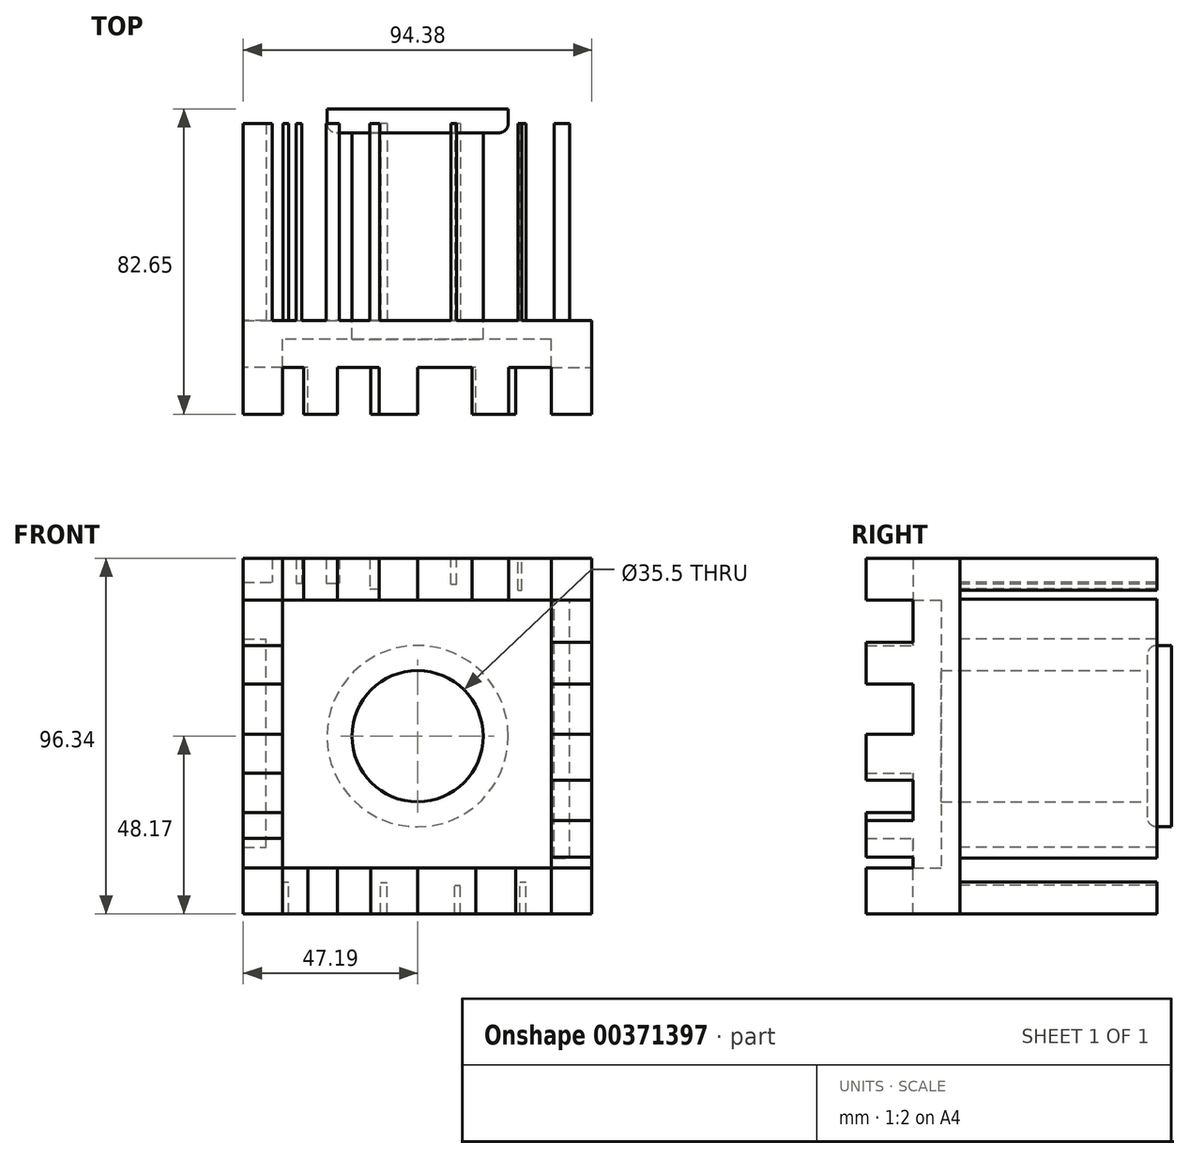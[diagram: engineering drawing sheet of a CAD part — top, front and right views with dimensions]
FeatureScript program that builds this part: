
annotation { "Feature Type Name" : "Feature", "Feature Type Description" : "" }
export const myFeature = defineFeature(function(context is Context, id is Id, definition is map)
    precondition{}
    {
        {
            var Q0;
            Q0=qCreatedBy(makeId("Front.planeOp"),FACE);
            var sketch = newSketch(context, id + "F0", { "sketchPlane" : qUnion([Q0])});
            skCircle(sketch, "E0", {"center": v(0, 0) * mm, "radius": 24.55 * mm});
            skSolve(sketch);
        }
        {
            var Q0;
            Q0 = qSketchRegion(id + "F0", true);
            extrude(context, id + "F1", {"entities" : qUnion([Q0]), "depth" : 6.45 * mm});
        }
        {
            var Q0;
            Q0=makeQuery(id+"F1.opExtrude","CAP_FACE",FACE,{"disambiguationData":[OSD([sQuery(id+"F0.wireOp",EDGE,"E0")])],"isStart":false});
            var sketch = newSketch(context, id + "F2", { "sketchPlane" : qUnion([Q0])});
            skCircle(sketch, "E1", {"center": v(0, 0) * mm, "radius": 17.75 * mm});
            skSolve(sketch);
        }
        {
            var Q0;
            Q0 = qSketchRegion(id + "F2", true);
            extrude(context, id + "F3", {"entities" : qUnion([Q0]), "operationType" : NewBodyOperationType.ADD, "depth" : 50.8 * mm});
        }
        {
            var Q0;
            Q0=makeQuery(id+"F3.opExtrude","CAP_FACE",FACE,{"disambiguationData":[OSD([sQuery(id+"F2.wireOp",EDGE,"E1")])],"isStart":false});
            var sketch = newSketch(context, id + "F4", { "sketchPlane" : qUnion([Q0])});
            skLineSegment(sketch, "E2.bottom", {"start": v(47.2, -48.17) * mm, "end": v(-47.2, -48.17) * mm});
            skLineSegment(sketch, "E2.top", {"start": v(47.2, 48.17) * mm, "end": v(-47.2, 48.17) * mm});
            skLineSegment(sketch, "E2.left", {"start": v(47.2, -48.17) * mm, "end": v(47.2, 48.17) * mm});
            skLineSegment(sketch, "E2.right", {"start": v(-47.2, -48.17) * mm, "end": v(-47.2, 48.17) * mm});
            skPoint(sketch, "E2.middle", {"position": v(0, 0) * mm});
            skSolve(sketch);
        }
        {
            var Q0;
            Q0=makeQuery(id+"F4.imprint","IMPRINT",FACE,{"disambiguationData":[TD([[makeQuery(id+"F4.imprint","IMPRINT",EDGE,{"derivedFrom":sQuery(id+"F4.wireOp",EDGE,"E2.bottom")}),-1.0]])]});
            extrude(context, id + "F5", {"entities" : qUnion([Q0]), "depth" : 5.08 * mm});
        }
        {
            var Q0;
            Q0=makeQuery(id+"F5.opExtrude","CAP_FACE",FACE,{"disambiguationData":[OSD([sQuery(id+"F2.wireOp",EDGE,"E1"),sQuery(id+"F4.wireOp",EDGE,"E2.bottom"),sQuery(id+"F4.wireOp",EDGE,"E2.top"),sQuery(id+"F4.wireOp",EDGE,"E2.left"),sQuery(id+"F4.wireOp",EDGE,"E2.right")])],"isStart":false});
            var sketch = newSketch(context, id + "F6", { "sketchPlane" : qUnion([Q0])});
            skLineSegment(sketch, "E3.bottom", {"start": v(-47.2, 48.17) * mm, "end": v(-36.6, 48.17) * mm});
            skLineSegment(sketch, "E3.top", {"start": v(-47.2, -48.17) * mm, "end": v(-36.6, -48.17) * mm});
            skLineSegment(sketch, "E3.left", {"start": v(-47.2, 48.17) * mm, "end": v(-47.2, -48.17) * mm});
            skLineSegment(sketch, "E3.right", {"start": v(-36.6, 48.17) * mm, "end": v(-36.6, -48.17) * mm});
            skLineSegment(sketch, "E4.bottom", {"start": v(47.2, -48.17) * mm, "end": v(-36.6, -48.17) * mm});
            skLineSegment(sketch, "E4.top", {"start": v(47.2, -35.68) * mm, "end": v(-36.6, -35.68) * mm});
            skLineSegment(sketch, "E4.left", {"start": v(47.2, -48.17) * mm, "end": v(47.2, -35.68) * mm});
            skLineSegment(sketch, "E4.right", {"start": v(-36.6, -48.17) * mm, "end": v(-36.6, -35.68) * mm});
            skLineSegment(sketch, "E5.bottom", {"start": v(47.2, 48.17) * mm, "end": v(-36.6, 48.17) * mm});
            skLineSegment(sketch, "E5.top", {"start": v(47.2, 36.8) * mm, "end": v(-36.6, 36.8) * mm});
            skLineSegment(sketch, "E5.left", {"start": v(47.2, 48.17) * mm, "end": v(47.2, 36.8) * mm});
            skLineSegment(sketch, "E5.right", {"start": v(-36.6, 48.17) * mm, "end": v(-36.6, 36.8) * mm});
            skLineSegment(sketch, "E6.bottom", {"start": v(47.2, 36.8) * mm, "end": v(36.19, 36.8) * mm});
            skLineSegment(sketch, "E6.top", {"start": v(47.2, -35.68) * mm, "end": v(36.19, -35.68) * mm});
            skLineSegment(sketch, "E6.left", {"start": v(47.2, 36.8) * mm, "end": v(47.2, -35.68) * mm});
            skLineSegment(sketch, "E6.right", {"start": v(36.19, 36.8) * mm, "end": v(36.19, -35.68) * mm});
            skSolve(sketch);
        }
        {
            var Q0;
            Q0 = qSketchRegion(id + "F6", true);
            extrude(context, id + "F7", {"entities" : qUnion([Q0]), "operationType" : NewBodyOperationType.ADD, "depth" : 7.62 * mm});
        }
        {
            var Q0;
            Q0=makeQuery(id+"F7.opExtrude","CAP_FACE",FACE,{"disambiguationData":[OSD([sQuery(id+"F6.wireOp",EDGE,"E3.bottom"),sQuery(id+"F6.wireOp",EDGE,"E3.top"),sQuery(id+"F6.wireOp",EDGE,"E3.left"),sQuery(id+"F6.wireOp",EDGE,"E3.right"),sQuery(id+"F6.wireOp",EDGE,"E4.bottom"),sQuery(id+"F6.wireOp",EDGE,"E4.top"),sQuery(id+"F6.wireOp",EDGE,"E4.left"),sQuery(id+"F6.wireOp",EDGE,"E5.bottom"),sQuery(id+"F6.wireOp",EDGE,"E5.top"),sQuery(id+"F6.wireOp",EDGE,"E5.left"),sQuery(id+"F6.wireOp",EDGE,"E6.left"),sQuery(id+"F6.wireOp",EDGE,"E6.right")])],"isStart":false});
            var sketch = newSketch(context, id + "F8", { "sketchPlane" : qUnion([Q0])});
            skLineSegment(sketch, "E7.bottom", {"start": v(47.2, 48.17) * mm, "end": v(36.19, 48.17) * mm});
            skLineSegment(sketch, "E7.top", {"start": v(47.2, 36.8) * mm, "end": v(36.19, 36.8) * mm});
            skLineSegment(sketch, "E7.left", {"start": v(47.2, 48.17) * mm, "end": v(47.2, 36.8) * mm});
            skLineSegment(sketch, "E7.right", {"start": v(36.19, 48.17) * mm, "end": v(36.19, 36.8) * mm});
            skLineSegment(sketch, "E8.bottom", {"start": v(24.7, 48.17) * mm, "end": v(14.71, 48.17) * mm});
            skLineSegment(sketch, "E8.top", {"start": v(24.7, 36.8) * mm, "end": v(14.71, 36.8) * mm});
            skLineSegment(sketch, "E8.left", {"start": v(24.7, 48.17) * mm, "end": v(24.7, 36.8) * mm});
            skLineSegment(sketch, "E8.right", {"start": v(14.71, 48.17) * mm, "end": v(14.71, 36.8) * mm});
            skLineSegment(sketch, "E9.bottom", {"start": v(0, 48.17) * mm, "end": v(-10.43, 48.17) * mm});
            skLineSegment(sketch, "E9.top", {"start": v(0, 36.8) * mm, "end": v(-10.43, 36.8) * mm});
            skLineSegment(sketch, "E9.left", {"start": v(0, 48.17) * mm, "end": v(0, 36.8) * mm});
            skLineSegment(sketch, "E9.right", {"start": v(-10.43, 48.17) * mm, "end": v(-10.43, 36.8) * mm});
            skLineSegment(sketch, "E10.bottom", {"start": v(-21.71, 48.17) * mm, "end": v(-30.9, 48.17) * mm});
            skLineSegment(sketch, "E10.top", {"start": v(-21.71, 36.8) * mm, "end": v(-30.9, 36.8) * mm});
            skLineSegment(sketch, "E10.left", {"start": v(-21.71, 48.17) * mm, "end": v(-21.71, 36.8) * mm});
            skLineSegment(sketch, "E10.right", {"start": v(-30.9, 48.17) * mm, "end": v(-30.9, 36.8) * mm});
            skLineSegment(sketch, "E11.bottom", {"start": v(-36.6, 36.8) * mm, "end": v(-47.2, 36.8) * mm});
            skLineSegment(sketch, "E11.top", {"start": v(-36.6, 48.17) * mm, "end": v(-47.2, 48.17) * mm});
            skLineSegment(sketch, "E11.left", {"start": v(-36.6, 36.8) * mm, "end": v(-36.6, 48.17) * mm});
            skLineSegment(sketch, "E11.right", {"start": v(-47.2, 36.8) * mm, "end": v(-47.2, 48.17) * mm});
            skLineSegment(sketch, "E12.bottom", {"start": v(-36.6, 24.51) * mm, "end": v(-47.2, 24.51) * mm});
            skLineSegment(sketch, "E12.top", {"start": v(-36.6, 14.1) * mm, "end": v(-47.2, 14.1) * mm});
            skLineSegment(sketch, "E12.left", {"start": v(-36.6, 24.51) * mm, "end": v(-36.6, 14.1) * mm});
            skLineSegment(sketch, "E12.right", {"start": v(-47.2, 24.51) * mm, "end": v(-47.2, 14.1) * mm});
            skLineSegment(sketch, "E13.bottom", {"start": v(-36.6, 0.56) * mm, "end": v(-47.2, 0.56) * mm});
            skLineSegment(sketch, "E13.top", {"start": v(-36.6, -10.02) * mm, "end": v(-47.2, -10.02) * mm});
            skLineSegment(sketch, "E13.left", {"start": v(-36.6, 0.56) * mm, "end": v(-36.6, -10.02) * mm});
            skLineSegment(sketch, "E13.right", {"start": v(-47.2, 0.56) * mm, "end": v(-47.2, -10.02) * mm});
            skLineSegment(sketch, "E14.bottom", {"start": v(-36.6, -20.68) * mm, "end": v(-47.2, -20.68) * mm});
            skLineSegment(sketch, "E14.top", {"start": v(-36.6, -27.62) * mm, "end": v(-47.2, -27.62) * mm});
            skLineSegment(sketch, "E14.left", {"start": v(-36.6, -20.68) * mm, "end": v(-36.6, -27.62) * mm});
            skLineSegment(sketch, "E14.right", {"start": v(-47.2, -20.68) * mm, "end": v(-47.2, -27.62) * mm});
            skLineSegment(sketch, "E15.bottom", {"start": v(-36.6, -35.68) * mm, "end": v(-47.2, -35.68) * mm});
            skLineSegment(sketch, "E15.top", {"start": v(-36.6, -48.17) * mm, "end": v(-47.2, -48.17) * mm});
            skLineSegment(sketch, "E15.left", {"start": v(-36.6, -35.68) * mm, "end": v(-36.6, -48.17) * mm});
            skLineSegment(sketch, "E15.right", {"start": v(-47.2, -35.68) * mm, "end": v(-47.2, -48.17) * mm});
            skLineSegment(sketch, "E16.bottom", {"start": v(36.19, 25.4) * mm, "end": v(47.2, 25.4) * mm});
            skLineSegment(sketch, "E16.top", {"start": v(36.19, 14.16) * mm, "end": v(47.2, 14.16) * mm});
            skLineSegment(sketch, "E16.left", {"start": v(36.19, 25.4) * mm, "end": v(36.19, 14.16) * mm});
            skLineSegment(sketch, "E16.right", {"start": v(47.2, 25.4) * mm, "end": v(47.2, 14.16) * mm});
            skLineSegment(sketch, "E17.bottom", {"start": v(36.19, 0.56) * mm, "end": v(47.2, 0.56) * mm});
            skLineSegment(sketch, "E17.top", {"start": v(36.19, -11.97) * mm, "end": v(47.2, -11.97) * mm});
            skLineSegment(sketch, "E17.left", {"start": v(36.19, 0.56) * mm, "end": v(36.19, -11.97) * mm});
            skLineSegment(sketch, "E17.right", {"start": v(47.2, 0.56) * mm, "end": v(47.2, -11.97) * mm});
            skLineSegment(sketch, "E18.bottom", {"start": v(36.19, -22.9) * mm, "end": v(47.2, -22.9) * mm});
            skLineSegment(sketch, "E18.top", {"start": v(36.19, -32.7) * mm, "end": v(47.2, -32.7) * mm});
            skLineSegment(sketch, "E18.left", {"start": v(36.19, -22.9) * mm, "end": v(36.19, -32.7) * mm});
            skLineSegment(sketch, "E18.right", {"start": v(47.2, -22.9) * mm, "end": v(47.2, -32.7) * mm});
            skLineSegment(sketch, "E19.bottom", {"start": v(47.2, -48.17) * mm, "end": v(36.19, -48.17) * mm});
            skLineSegment(sketch, "E19.top", {"start": v(47.2, -35.68) * mm, "end": v(36.19, -35.68) * mm});
            skLineSegment(sketch, "E19.left", {"start": v(47.2, -48.17) * mm, "end": v(47.2, -35.68) * mm});
            skLineSegment(sketch, "E19.right", {"start": v(36.19, -48.17) * mm, "end": v(36.19, -35.68) * mm});
            skLineSegment(sketch, "E20.bottom", {"start": v(26.62, -48.17) * mm, "end": v(15.76, -48.17) * mm});
            skLineSegment(sketch, "E20.top", {"start": v(26.62, -35.68) * mm, "end": v(15.76, -35.68) * mm});
            skLineSegment(sketch, "E20.left", {"start": v(26.62, -48.17) * mm, "end": v(26.62, -35.68) * mm});
            skLineSegment(sketch, "E20.right", {"start": v(15.76, -48.17) * mm, "end": v(15.76, -35.68) * mm});
            skLineSegment(sketch, "E21.bottom", {"start": v(0, -48.17) * mm, "end": v(-12.67, -48.17) * mm});
            skLineSegment(sketch, "E21.top", {"start": v(0, -35.68) * mm, "end": v(-12.67, -35.68) * mm});
            skLineSegment(sketch, "E21.left", {"start": v(0, -48.17) * mm, "end": v(0, -35.68) * mm});
            skLineSegment(sketch, "E21.right", {"start": v(-12.67, -48.17) * mm, "end": v(-12.67, -35.68) * mm});
            skLineSegment(sketch, "E22.bottom", {"start": v(-21.71, -48.17) * mm, "end": v(-29.71, -48.17) * mm});
            skLineSegment(sketch, "E22.top", {"start": v(-21.71, -35.68) * mm, "end": v(-29.71, -35.68) * mm});
            skLineSegment(sketch, "E22.left", {"start": v(-21.71, -48.17) * mm, "end": v(-21.71, -35.68) * mm});
            skLineSegment(sketch, "E22.right", {"start": v(-29.71, -48.17) * mm, "end": v(-29.71, -35.68) * mm});
            skSolve(sketch);
        }
        {
            var Q0;
            Q0 = qSketchRegion(id + "F8", true);
            extrude(context, id + "F9", {"entities" : qUnion([Q0]), "operationType" : NewBodyOperationType.ADD, "depth" : 12.7 * mm});
        }
        {
            var Q0;
            Q0=makeQuery(id+"F5.opExtrude","CAP_FACE",FACE,{"disambiguationData":[OSD([sQuery(id+"F2.wireOp",EDGE,"E1"),sQuery(id+"F4.wireOp",EDGE,"E2.bottom"),sQuery(id+"F4.wireOp",EDGE,"E2.top"),sQuery(id+"F4.wireOp",EDGE,"E2.left"),sQuery(id+"F4.wireOp",EDGE,"E2.right")])],"isStart":true});
            var sketch = newSketch(context, id + "F10", { "sketchPlane" : qUnion([Q0])});
            skLineSegment(sketch, "E23.bottom", {"start": v(9.95, -48.17) * mm, "end": v(8.18, -48.17) * mm});
            skLineSegment(sketch, "E23.top", {"start": v(9.95, -39.55) * mm, "end": v(8.18, -39.55) * mm});
            skLineSegment(sketch, "E23.left", {"start": v(9.95, -48.17) * mm, "end": v(9.95, -39.55) * mm});
            skLineSegment(sketch, "E23.right", {"start": v(8.18, -48.17) * mm, "end": v(8.18, -39.55) * mm});
            skLineSegment(sketch, "E24.bottom", {"start": v(-10.05, -48.17) * mm, "end": v(-11.57, -48.17) * mm});
            skLineSegment(sketch, "E24.top", {"start": v(-10.05, -40.4) * mm, "end": v(-11.57, -40.4) * mm});
            skLineSegment(sketch, "E24.left", {"start": v(-10.05, -48.17) * mm, "end": v(-10.05, -40.4) * mm});
            skLineSegment(sketch, "E24.right", {"start": v(-11.57, -48.17) * mm, "end": v(-11.57, -40.4) * mm});
            skLineSegment(sketch, "E25.bottom", {"start": v(-27.74, -48.17) * mm, "end": v(-29.37, -48.17) * mm});
            skLineSegment(sketch, "E25.top", {"start": v(-27.74, -39.52) * mm, "end": v(-29.37, -39.52) * mm});
            skLineSegment(sketch, "E25.left", {"start": v(-27.74, -48.17) * mm, "end": v(-27.74, -39.52) * mm});
            skLineSegment(sketch, "E25.right", {"start": v(-29.37, -48.17) * mm, "end": v(-29.37, -39.52) * mm});
            skLineSegment(sketch, "E26.bottom", {"start": v(36.38, -48.17) * mm, "end": v(34.96, -48.17) * mm});
            skLineSegment(sketch, "E26.top", {"start": v(36.38, -39.45) * mm, "end": v(34.96, -39.45) * mm});
            skLineSegment(sketch, "E26.left", {"start": v(36.38, -48.17) * mm, "end": v(36.38, -39.45) * mm});
            skLineSegment(sketch, "E26.right", {"start": v(34.96, -48.17) * mm, "end": v(34.96, -39.45) * mm});
            skLineSegment(sketch, "E27.bottom", {"start": v(-27.2, 39.51) * mm, "end": v(-28.2, 39.51) * mm});
            skLineSegment(sketch, "E27.top", {"start": v(-27.2, 48.17) * mm, "end": v(-28.2, 48.17) * mm});
            skLineSegment(sketch, "E27.left", {"start": v(-27.2, 39.51) * mm, "end": v(-27.2, 48.17) * mm});
            skLineSegment(sketch, "E27.right", {"start": v(-28.2, 39.51) * mm, "end": v(-28.2, 48.17) * mm});
            skLineSegment(sketch, "E28.bottom", {"start": v(-9.07, 41.1) * mm, "end": v(-10.58, 41.1) * mm});
            skLineSegment(sketch, "E28.top", {"start": v(-9.07, 48.17) * mm, "end": v(-10.58, 48.17) * mm});
            skLineSegment(sketch, "E28.left", {"start": v(-9.07, 41.1) * mm, "end": v(-9.07, 48.17) * mm});
            skLineSegment(sketch, "E28.right", {"start": v(-10.58, 41.1) * mm, "end": v(-10.58, 48.17) * mm});
            skLineSegment(sketch, "E29.bottom", {"start": v(47.2, 48.17) * mm, "end": v(39.32, 48.17) * mm});
            skLineSegment(sketch, "E29.top", {"start": v(47.2, 41.64) * mm, "end": v(39.32, 41.64) * mm});
            skLineSegment(sketch, "E29.left", {"start": v(47.2, 48.17) * mm, "end": v(47.2, 41.64) * mm});
            skLineSegment(sketch, "E29.right", {"start": v(39.32, 48.17) * mm, "end": v(39.32, 41.64) * mm});
            skLineSegment(sketch, "E30.bottom", {"start": v(32.94, 48.17) * mm, "end": v(31.32, 48.17) * mm});
            skLineSegment(sketch, "E30.top", {"start": v(32.94, 41.42) * mm, "end": v(31.32, 41.42) * mm});
            skLineSegment(sketch, "E30.left", {"start": v(32.94, 48.17) * mm, "end": v(32.94, 41.42) * mm});
            skLineSegment(sketch, "E30.right", {"start": v(31.32, 48.17) * mm, "end": v(31.32, 41.42) * mm});
            skLineSegment(sketch, "E31.bottom", {"start": v(24.76, 48.17) * mm, "end": v(21.16, 48.17) * mm});
            skLineSegment(sketch, "E31.top", {"start": v(24.76, 41.42) * mm, "end": v(21.16, 41.42) * mm});
            skLineSegment(sketch, "E31.left", {"start": v(24.76, 48.17) * mm, "end": v(24.76, 41.42) * mm});
            skLineSegment(sketch, "E31.right", {"start": v(21.16, 48.17) * mm, "end": v(21.16, 41.42) * mm});
            skLineSegment(sketch, "E32.bottom", {"start": v(12.96, 48.17) * mm, "end": v(10.26, 48.17) * mm});
            skLineSegment(sketch, "E32.top", {"start": v(12.96, 39.85) * mm, "end": v(10.26, 39.85) * mm});
            skLineSegment(sketch, "E32.left", {"start": v(12.96, 48.17) * mm, "end": v(12.96, 39.85) * mm});
            skLineSegment(sketch, "E32.right", {"start": v(10.26, 48.17) * mm, "end": v(10.26, 39.85) * mm});
            skLineSegment(sketch, "E33.bottom", {"start": v(-37.02, -33.02) * mm, "end": v(-41.14, -33.02) * mm});
            skLineSegment(sketch, "E33.top", {"start": v(-37.02, 37.05) * mm, "end": v(-41.14, 37.05) * mm});
            skLineSegment(sketch, "E33.left", {"start": v(-37.02, -33.02) * mm, "end": v(-37.02, 37.05) * mm});
            skLineSegment(sketch, "E33.right", {"start": v(-41.14, -33.02) * mm, "end": v(-41.14, 37.05) * mm});
            skLineSegment(sketch, "E34.bottom", {"start": v(47.2, -30.1) * mm, "end": v(41.02, -30.1) * mm});
            skLineSegment(sketch, "E34.top", {"start": v(47.2, 26.3) * mm, "end": v(41.02, 26.3) * mm});
            skLineSegment(sketch, "E34.left", {"start": v(47.2, -30.1) * mm, "end": v(47.2, 26.3) * mm});
            skLineSegment(sketch, "E34.right", {"start": v(41.02, -30.1) * mm, "end": v(41.02, 26.3) * mm});
            skSolve(sketch);
        }
        {
            var Q0;
            Q0=makeQuery(id+"F10.imprint","IMPRINT",FACE,{"disambiguationData":[TD([[makeQuery(id+"F10.imprint","IMPRINT",EDGE,{"derivedFrom":sQuery(id+"F10.wireOp",EDGE,"E34.bottom")}),-1.0]])]});
            var Q1;
            Q1=makeQuery(id+"F10.imprint","IMPRINT",FACE,{"disambiguationData":[TD([[makeQuery(id+"F10.imprint","IMPRINT",EDGE,{"derivedFrom":sQuery(id+"F10.wireOp",EDGE,"E26.bottom")}),1.0]])]});
            var Q2;
            Q2=makeQuery(id+"F10.imprint","IMPRINT",FACE,{"disambiguationData":[TD([[makeQuery(id+"F10.imprint","IMPRINT",EDGE,{"derivedFrom":sQuery(id+"F10.wireOp",EDGE,"E23.bottom")}),1.0]])]});
            var Q3;
            Q3=makeQuery(id+"F10.imprint","IMPRINT",FACE,{"disambiguationData":[TD([[makeQuery(id+"F10.imprint","IMPRINT",EDGE,{"derivedFrom":sQuery(id+"F10.wireOp",EDGE,"E24.bottom")}),1.0]])]});
            var Q4;
            Q4=makeQuery(id+"F10.imprint","IMPRINT",FACE,{"disambiguationData":[TD([[makeQuery(id+"F10.imprint","IMPRINT",EDGE,{"derivedFrom":sQuery(id+"F10.wireOp",EDGE,"E25.bottom")}),1.0]])]});
            var Q5;
            Q5=makeQuery(id+"F10.imprint","IMPRINT",FACE,{"disambiguationData":[TD([[makeQuery(id+"F10.imprint","IMPRINT",EDGE,{"derivedFrom":sQuery(id+"F10.wireOp",EDGE,"E33.bottom")}),-1.0]])]});
            var Q6;
            Q6=makeQuery(id+"F10.imprint","IMPRINT",FACE,{"disambiguationData":[TD([[makeQuery(id+"F10.imprint","IMPRINT",EDGE,{"derivedFrom":sQuery(id+"F10.wireOp",EDGE,"E27.bottom")}),-1.0]])]});
            var Q7;
            Q7=makeQuery(id+"F10.imprint","IMPRINT",FACE,{"disambiguationData":[TD([[makeQuery(id+"F10.imprint","IMPRINT",EDGE,{"derivedFrom":sQuery(id+"F10.wireOp",EDGE,"E28.bottom")}),-1.0]])]});
            var Q8;
            Q8=makeQuery(id+"F10.imprint","IMPRINT",FACE,{"disambiguationData":[TD([[makeQuery(id+"F10.imprint","IMPRINT",EDGE,{"derivedFrom":sQuery(id+"F10.wireOp",EDGE,"E32.bottom")}),-1.0]])]});
            var Q9;
            Q9=makeQuery(id+"F10.imprint","IMPRINT",FACE,{"disambiguationData":[TD([[makeQuery(id+"F10.imprint","IMPRINT",EDGE,{"derivedFrom":sQuery(id+"F10.wireOp",EDGE,"E31.bottom")}),-1.0]])]});
            var Q10;
            Q10=makeQuery(id+"F10.imprint","IMPRINT",FACE,{"disambiguationData":[TD([[makeQuery(id+"F10.imprint","IMPRINT",EDGE,{"derivedFrom":sQuery(id+"F10.wireOp",EDGE,"E29.bottom")}),-1.0]])]});
            var Q11;
            Q11=makeQuery(id+"F10.imprint","IMPRINT",FACE,{"disambiguationData":[TD([[makeQuery(id+"F10.imprint","IMPRINT",EDGE,{"derivedFrom":sQuery(id+"F10.wireOp",EDGE,"E30.bottom")}),-1.0]])]});
            extrude(context, id + "F11", {"entities" : qUnion([Q0, Q1, Q2, Q3, Q4, Q5, Q6, Q7, Q8, Q9, Q10, Q11]), "operationType" : NewBodyOperationType.ADD, "depth" : 53.34 * mm});
        }
        {
            var Q0;
            Q0=makeQuery(id+"F1.opExtrude","CAP_EDGE",EDGE,{"disambiguationData":[OSD([sQuery(id+"F0.wireOp",EDGE,"E0")])],"isStart":false});
            fillet(context, id + "F12", {"entities" : qUnion([Q0]), "radius" : 2.54 * mm, "tangentPropagation" : true, "allowEdgeOverflow" : false});
        }
    });
